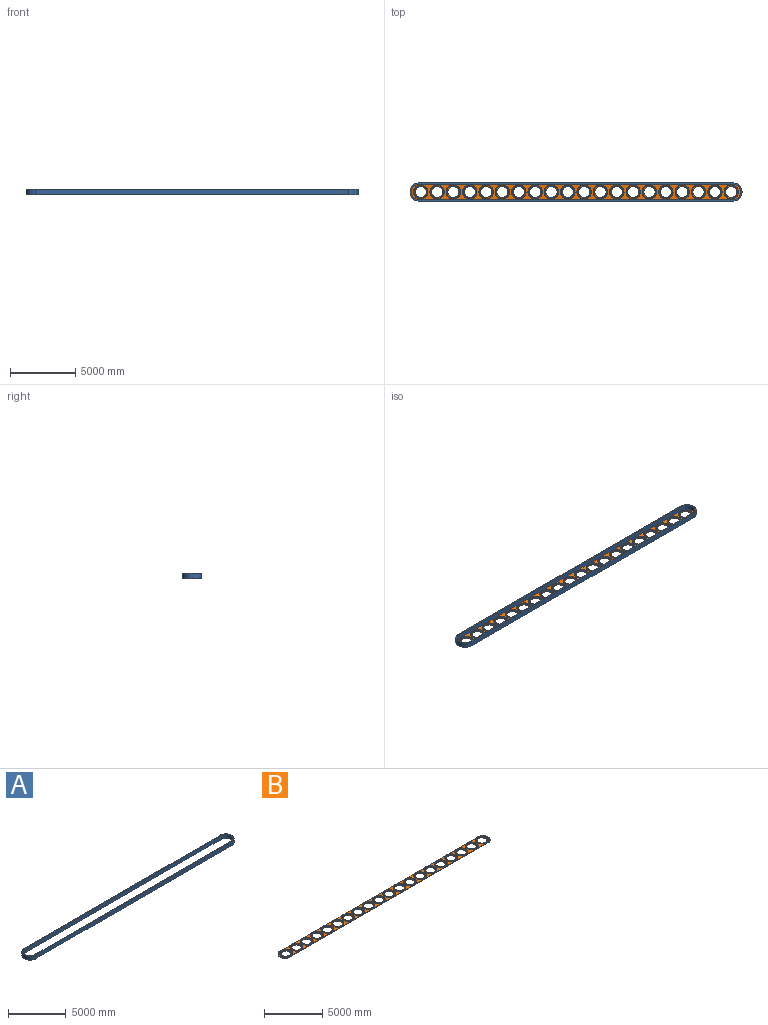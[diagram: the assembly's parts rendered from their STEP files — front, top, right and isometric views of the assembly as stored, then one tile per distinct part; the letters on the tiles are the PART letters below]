
ASSEMBLY  parts=2 mates=1
PART A: 10 faces, bbox 25400x1400x400 mm
  f0: cylinder r=600mm len=1200mm, axis (0,0,-1), area 753982.2mm2, adj f1,f7,f8,f9
  f1: plane 24000x400mm, normal (0,-1,0), area 9600000mm2, adj f0,f2,f8,f9
  f2: cylinder r=600mm len=1200mm, axis (0,0,-1), area 753982.2mm2, adj f1,f7,f8,f9
  f3: plane 24000x400mm, normal (0,-1,0), area 9600000mm2, adj f4,f6,f8,f9
  f4: cylinder r=700mm len=1400mm, axis (0,0,-1), area 879645.9mm2, adj f3,f5,f8,f9
  f5: plane 24000x400mm, normal (0,1,0), area 9600000mm2, adj f4,f6,f8,f9
  f6: cylinder r=700mm len=1400mm, axis (0,0,-1), area 879645.9mm2, adj f3,f5,f8,f9
  f7: plane 24000x400mm, normal (0,1,0), area 9600000mm2, adj f0,f2,f8,f9
  f8: plane 25400x1400mm, normal (0,0,1), area 5208407mm2, adj f0,f1,f2,f3,f4,f5,f6,f7
  f9: plane 25400x1400mm, normal (0,0,-1), area 5208407mm2, adj f0,f1,f2,f3,f4,f5,f6,f7
PART B: 106 faces, bbox 25200x1200x100 mm
  f0: plane 24000x50mm, normal (0,1,0), area 1200000mm2, adj f1,f3,f4,f5
  f1: cylinder r=600mm len=1200mm, axis (0,0,-1), area 94247.8mm2, adj f0,f2,f4,f5
  f2: plane 24000x50mm, normal (0,-1,0), area 1200000mm2, adj f1,f3,f4,f5
  f3: cylinder r=600mm len=1200mm, axis (0,0,-1), area 94247.8mm2, adj f0,f2,f4,f5
  f4: plane 25200x1200mm, normal (0,0,1), area 10924337.8mm2, adj f0,f1,f2,f3,f7,f11,f15,f19
  f5: plane 25200x1200mm, normal (0,0,-1), area 18581969.9mm2, adj f0,f1,f2,f3,f86,f87,f88,f89
  f6: cylinder r=500mm len=1000mm, axis (0,0,-1), area 157079.6mm2, adj f8,f9
  f7: cylinder r=550mm len=1100mm, axis (0,0,-1), area 172787.6mm2, adj f4,f8
  f8: plane 1100x1100mm, normal (0,0,1), area 164933.6mm2, adj f6,f7
  f9: plane 1000x1000mm, normal (0,0,1), area 217948mm2, adj f6,f105
  f10: cylinder r=500mm len=1000mm, axis (0,0,-1), area 157079.6mm2, adj f12,f13
  f11: cylinder r=550mm len=1100mm, axis (0,0,-1), area 172787.6mm2, adj f4,f12
  f12: plane 1100x1100mm, normal (0,0,1), area 164933.6mm2, adj f10,f11
  f13: plane 1000x1000mm, normal (0,0,1), area 217948mm2, adj f10,f104
  f14: cylinder r=500mm len=1000mm, axis (0,0,-1), area 157079.6mm2, adj f16,f17
  f15: cylinder r=550mm len=1100mm, axis (0,0,-1), area 172787.6mm2, adj f4,f16
  f16: plane 1100x1100mm, normal (0,0,1), area 164933.6mm2, adj f14,f15
  f17: plane 1000x1000mm, normal (0,0,1), area 217948mm2, adj f14,f103
  f18: cylinder r=500mm len=1000mm, axis (0,0,-1), area 157079.6mm2, adj f20,f21
  f19: cylinder r=550mm len=1100mm, axis (0,0,-1), area 172787.6mm2, adj f4,f20
  f20: plane 1100x1100mm, normal (0,0,1), area 164933.6mm2, adj f18,f19
  f21: plane 1000x1000mm, normal (0,0,1), area 217948mm2, adj f18,f102
  f22: cylinder r=500mm len=1000mm, axis (0,0,-1), area 157079.6mm2, adj f24,f25
  f23: cylinder r=550mm len=1100mm, axis (0,0,-1), area 172787.6mm2, adj f4,f24
  f24: plane 1100x1100mm, normal (0,0,1), area 164933.6mm2, adj f22,f23
  f25: plane 1000x1000mm, normal (0,0,1), area 217948mm2, adj f22,f101
  f26: cylinder r=500mm len=1000mm, axis (0,0,-1), area 157079.6mm2, adj f28,f29
  f27: cylinder r=550mm len=1100mm, axis (0,0,-1), area 172787.6mm2, adj f4,f28
  f28: plane 1100x1100mm, normal (0,0,1), area 164933.6mm2, adj f26,f27
  f29: plane 1000x1000mm, normal (0,0,1), area 217948mm2, adj f26,f100
  f30: cylinder r=500mm len=1000mm, axis (0,0,-1), area 157079.6mm2, adj f32,f33
  f31: cylinder r=550mm len=1100mm, axis (0,0,-1), area 172787.6mm2, adj f4,f32
  f32: plane 1100x1100mm, normal (0,0,1), area 164933.6mm2, adj f30,f31
  f33: plane 1000x1000mm, normal (0,0,1), area 217948mm2, adj f30,f99
  f34: cylinder r=500mm len=1000mm, axis (0,0,-1), area 157079.6mm2, adj f36,f37
  f35: cylinder r=550mm len=1100mm, axis (0,0,-1), area 172787.6mm2, adj f4,f36
  f36: plane 1100x1100mm, normal (0,0,1), area 164933.6mm2, adj f34,f35
  f37: plane 1000x1000mm, normal (0,0,1), area 217948mm2, adj f34,f98
  f38: cylinder r=500mm len=1000mm, axis (0,0,-1), area 157079.6mm2, adj f40,f41
  f39: cylinder r=550mm len=1100mm, axis (0,0,-1), area 172787.6mm2, adj f4,f40
  f40: plane 1100x1100mm, normal (0,0,1), area 164933.6mm2, adj f38,f39
  f41: plane 1000x1000mm, normal (0,0,1), area 217948mm2, adj f38,f97
  f42: cylinder r=500mm len=1000mm, axis (0,0,-1), area 157079.6mm2, adj f44,f45
  f43: cylinder r=550mm len=1100mm, axis (0,0,-1), area 172787.6mm2, adj f4,f44
  f44: plane 1100x1100mm, normal (0,0,1), area 164933.6mm2, adj f42,f43
  f45: plane 1000x1000mm, normal (0,0,1), area 217948mm2, adj f42,f96
  f46: cylinder r=550mm len=1100mm, axis (0,0,-1), area 172787.6mm2, adj f4,f48
  f47: cylinder r=500mm len=1000mm, axis (0,0,-1), area 157079.6mm2, adj f48,f49
  f48: plane 1100x1100mm, normal (0,0,1), area 164933.6mm2, adj f46,f47
  f49: plane 1000x1000mm, normal (0,0,1), area 217948mm2, adj f47,f95
  f50: cylinder r=550mm len=1100mm, axis (0,0,-1), area 172787.6mm2, adj f4,f52
  f51: cylinder r=500mm len=1000mm, axis (0,0,-1), area 157079.6mm2, adj f52,f53
  f52: plane 1100x1100mm, normal (0,0,1), area 164933.6mm2, adj f50,f51
  f53: plane 1000x1000mm, normal (0,0,1), area 217948mm2, adj f51,f94
  f54: cylinder r=550mm len=1100mm, axis (0,0,-1), area 172787.6mm2, adj f4,f56
  f55: cylinder r=500mm len=1000mm, axis (0,0,-1), area 157079.6mm2, adj f56,f57
  f56: plane 1100x1100mm, normal (0,0,1), area 164933.6mm2, adj f54,f55
  f57: plane 1000x1000mm, normal (0,0,1), area 217948mm2, adj f55,f93
  f58: cylinder r=550mm len=1100mm, axis (0,0,-1), area 172787.6mm2, adj f4,f60
  f59: cylinder r=500mm len=1000mm, axis (0,0,-1), area 157079.6mm2, adj f60,f61
  f60: plane 1100x1100mm, normal (0,0,1), area 164933.6mm2, adj f58,f59
  f61: plane 1000x1000mm, normal (0,0,1), area 217948mm2, adj f59,f92
  f62: cylinder r=550mm len=1100mm, axis (0,0,-1), area 172787.6mm2, adj f4,f64
  f63: cylinder r=500mm len=1000mm, axis (0,0,-1), area 157079.6mm2, adj f64,f65
  f64: plane 1100x1100mm, normal (0,0,1), area 164933.6mm2, adj f62,f63
  f65: plane 1000x1000mm, normal (0,0,1), area 217948mm2, adj f63,f91
  f66: cylinder r=550mm len=1100mm, axis (0,0,-1), area 172787.6mm2, adj f4,f68
  f67: cylinder r=500mm len=1000mm, axis (0,0,-1), area 157079.6mm2, adj f68,f69
  f68: plane 1100x1100mm, normal (0,0,1), area 164933.6mm2, adj f66,f67
  f69: plane 1000x1000mm, normal (0,0,1), area 217948mm2, adj f67,f90
  f70: cylinder r=550mm len=1100mm, axis (0,0,-1), area 172787.6mm2, adj f4,f72
  f71: cylinder r=500mm len=1000mm, axis (0,0,-1), area 157079.6mm2, adj f72,f73
  f72: plane 1100x1100mm, normal (0,0,1), area 164933.6mm2, adj f70,f71
  f73: plane 1000x1000mm, normal (0,0,1), area 217948mm2, adj f71,f89
  f74: cylinder r=550mm len=1100mm, axis (0,0,-1), area 172787.6mm2, adj f4,f76
  f75: cylinder r=500mm len=1000mm, axis (0,0,-1), area 157079.6mm2, adj f76,f77
  f76: plane 1100x1100mm, normal (0,0,1), area 164933.6mm2, adj f74,f75
  f77: plane 1000x1000mm, normal (0,0,1), area 217948mm2, adj f75,f88
  f78: cylinder r=550mm len=1100mm, axis (0,0,-1), area 172787.6mm2, adj f4,f80
  f79: cylinder r=500mm len=1000mm, axis (0,0,-1), area 157079.6mm2, adj f80,f81
  f80: plane 1100x1100mm, normal (0,0,1), area 164933.6mm2, adj f78,f79
  f81: plane 1000x1000mm, normal (0,0,1), area 217948mm2, adj f79,f87
  f82: cylinder r=550mm len=1100mm, axis (0,0,-1), area 172787.6mm2, adj f4,f84
  f83: cylinder r=500mm len=1000mm, axis (0,0,-1), area 157079.6mm2, adj f84,f85
  f84: plane 1100x1100mm, normal (0,0,1), area 164933.6mm2, adj f82,f83
  f85: plane 1000x1000mm, normal (0,0,1), area 217948mm2, adj f83,f86
  f86: cylinder r=425mm len=850mm, axis (0,0,1), area 133517.7mm2, adj f5,f85
  f87: cylinder r=425mm len=850mm, axis (0,0,1), area 133517.7mm2, adj f5,f81
  f88: cylinder r=425mm len=850mm, axis (0,0,1), area 133517.7mm2, adj f5,f77
  f89: cylinder r=425mm len=850mm, axis (0,0,1), area 133517.7mm2, adj f5,f73
  f90: cylinder r=425mm len=850mm, axis (0,0,1), area 133517.7mm2, adj f5,f69
  f91: cylinder r=425mm len=850mm, axis (0,0,1), area 133517.7mm2, adj f5,f65
  f92: cylinder r=425mm len=850mm, axis (0,0,1), area 133517.7mm2, adj f5,f61
  f93: cylinder r=425mm len=850mm, axis (0,0,1), area 133517.7mm2, adj f5,f57
  f94: cylinder r=425mm len=850mm, axis (0,0,1), area 133517.7mm2, adj f5,f53
  f95: cylinder r=425mm len=850mm, axis (0,0,1), area 133517.7mm2, adj f5,f49
  f96: cylinder r=425mm len=850mm, axis (0,0,1), area 133517.7mm2, adj f5,f45
  f97: cylinder r=425mm len=850mm, axis (0,0,1), area 133517.7mm2, adj f5,f41
  f98: cylinder r=425mm len=850mm, axis (0,0,1), area 133517.7mm2, adj f5,f37
  f99: cylinder r=425mm len=850mm, axis (0,0,1), area 133517.7mm2, adj f5,f33
  f100: cylinder r=425mm len=850mm, axis (0,0,1), area 133517.7mm2, adj f5,f29
  f101: cylinder r=425mm len=850mm, axis (0,0,1), area 133517.7mm2, adj f5,f25
  f102: cylinder r=425mm len=850mm, axis (0,0,1), area 133517.7mm2, adj f5,f21
  f103: cylinder r=425mm len=850mm, axis (0,0,1), area 133517.7mm2, adj f5,f17
  f104: cylinder r=425mm len=850mm, axis (0,0,1), area 133517.7mm2, adj f5,f13
  f105: cylinder r=425mm len=850mm, axis (0,0,1), area 133517.7mm2, adj f5,f9
PLACE A at identity
PLACE B at identity
MATE slider B.f1 <-> A.f0  axis (0,0,-1) through (-12000,0,0)mm
